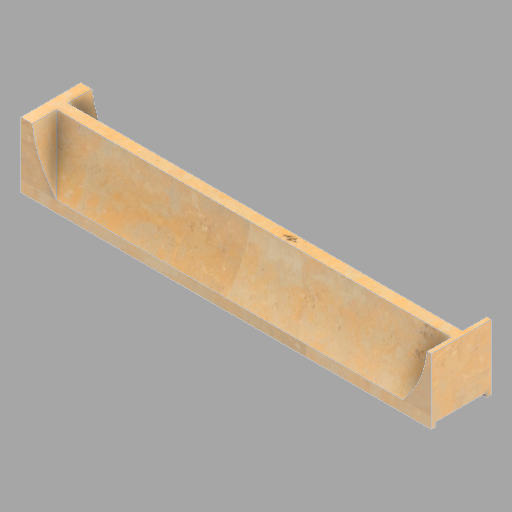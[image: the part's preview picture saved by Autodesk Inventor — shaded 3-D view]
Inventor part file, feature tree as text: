
AUTODESK INVENTOR PART (.ipt)
format: ipt  version: 2022.2 (Build 262287010, 287A)  size: 271,872 bytes
history: native  units: in
note: dims shown in document units (in); Inventor stores cm internally (conversion verified against a paired STEP export)
features: plane x1, extrude x1, sketch x1, other x1
ambient origin geometry x8: Origin, YZ Plane, XZ Plane, XY Plane, X Axis, Y Axis, Z Axis, Center Point
bodies: Solid1 (feature_tree)
feature tree (4):
  plane  "Work Plane1"
  extrude  "Extrusion1"  Depth=8.75in
  sketch  "Sketch1"  dims[d1=8.75in d2=8.75in d3=35.4375in d4=0.0in]
  other  "North (6)"
